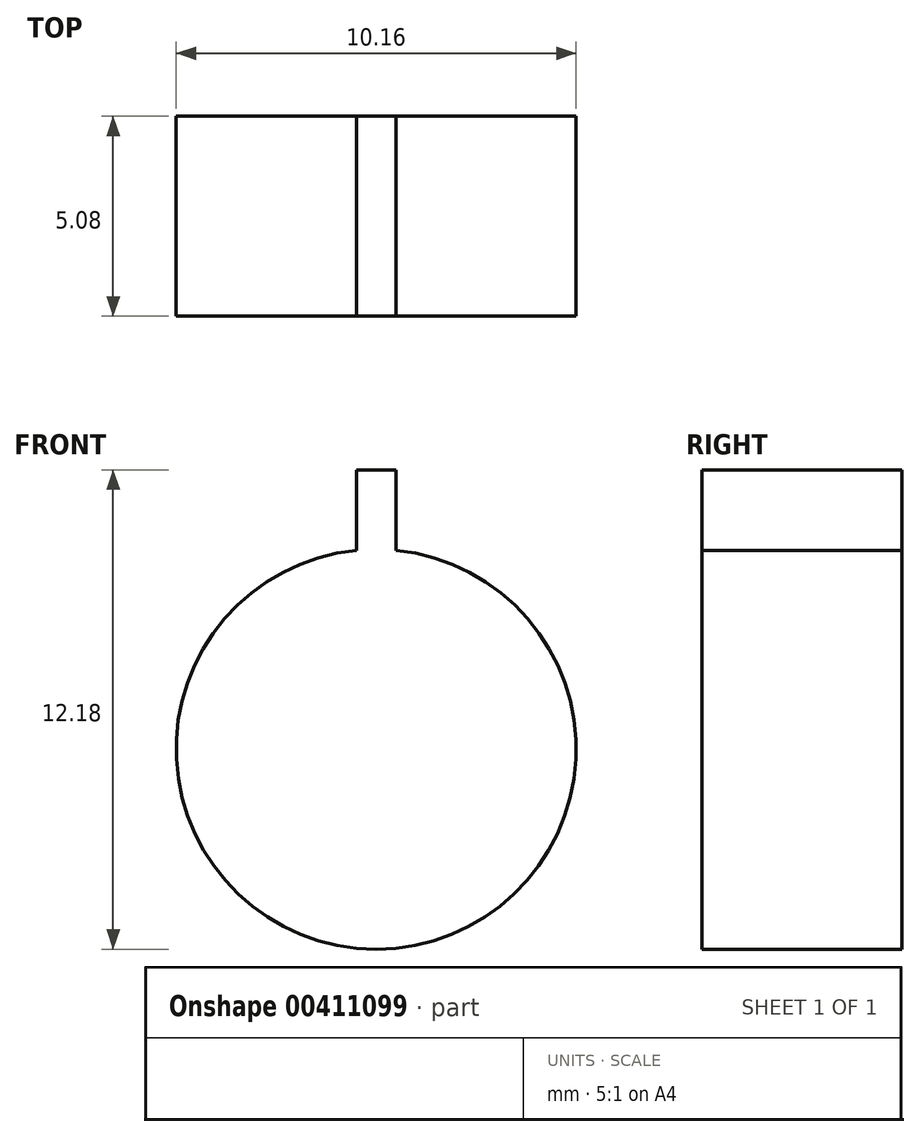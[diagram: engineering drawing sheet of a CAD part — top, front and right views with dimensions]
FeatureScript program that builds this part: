
annotation { "Feature Type Name" : "Feature", "Feature Type Description" : "" }
export const myFeature = defineFeature(function(context is Context, id is Id, definition is map)
    precondition{}
    {
        {
            var Q0;
            Q0=qCreatedBy(makeId("Front.planeOp"),FACE);
            var sketch = newSketch(context, id + "F0", { "sketchPlane" : qUnion([Q0])});
            skArc(sketch, "E0", {"start": v(-0.5, 5.06) * mm, "mid": v(0, -5.08) * mm, "end": v(0.5, 5.06) * mm});
            skLineSegment(sketch, "E1", {"start": v(0, 5.08) * mm, "end": v(0, 10.87) * mm, "construction": true});
            skLineSegment(sketch, "E2", {"start": v(-0.5, 5.06) * mm, "end": v(-0.5, 7.1) * mm});
            skLineSegment(sketch, "E3", {"start": v(-0.5, 7.1) * mm, "end": v(0, 7.1) * mm});
            skLineSegment(sketch, "E4.MirrorCS", {"start": v(0.5, 5.06) * mm, "end": v(0.5, 7.1) * mm});
            skLineSegment(sketch, "E5.MirrorCS", {"start": v(0.5, 7.1) * mm, "end": v(0, 7.1) * mm});
            skSolve(sketch);
        }
        {
            var Q0;
            Q0=makeQuery(id+"F0.imprint","IMPRINT",FACE,{"disambiguationData":[TD([[makeQuery(id+"F0.imprint","IMPRINT",EDGE,{"derivedFrom":sQuery(id+"F0.wireOp",EDGE,"E0")}),1.0]])]});
            extrude(context, id + "F1", {"entities" : qUnion([Q0]), "depth" : 5.08 * mm});
        }
    });
